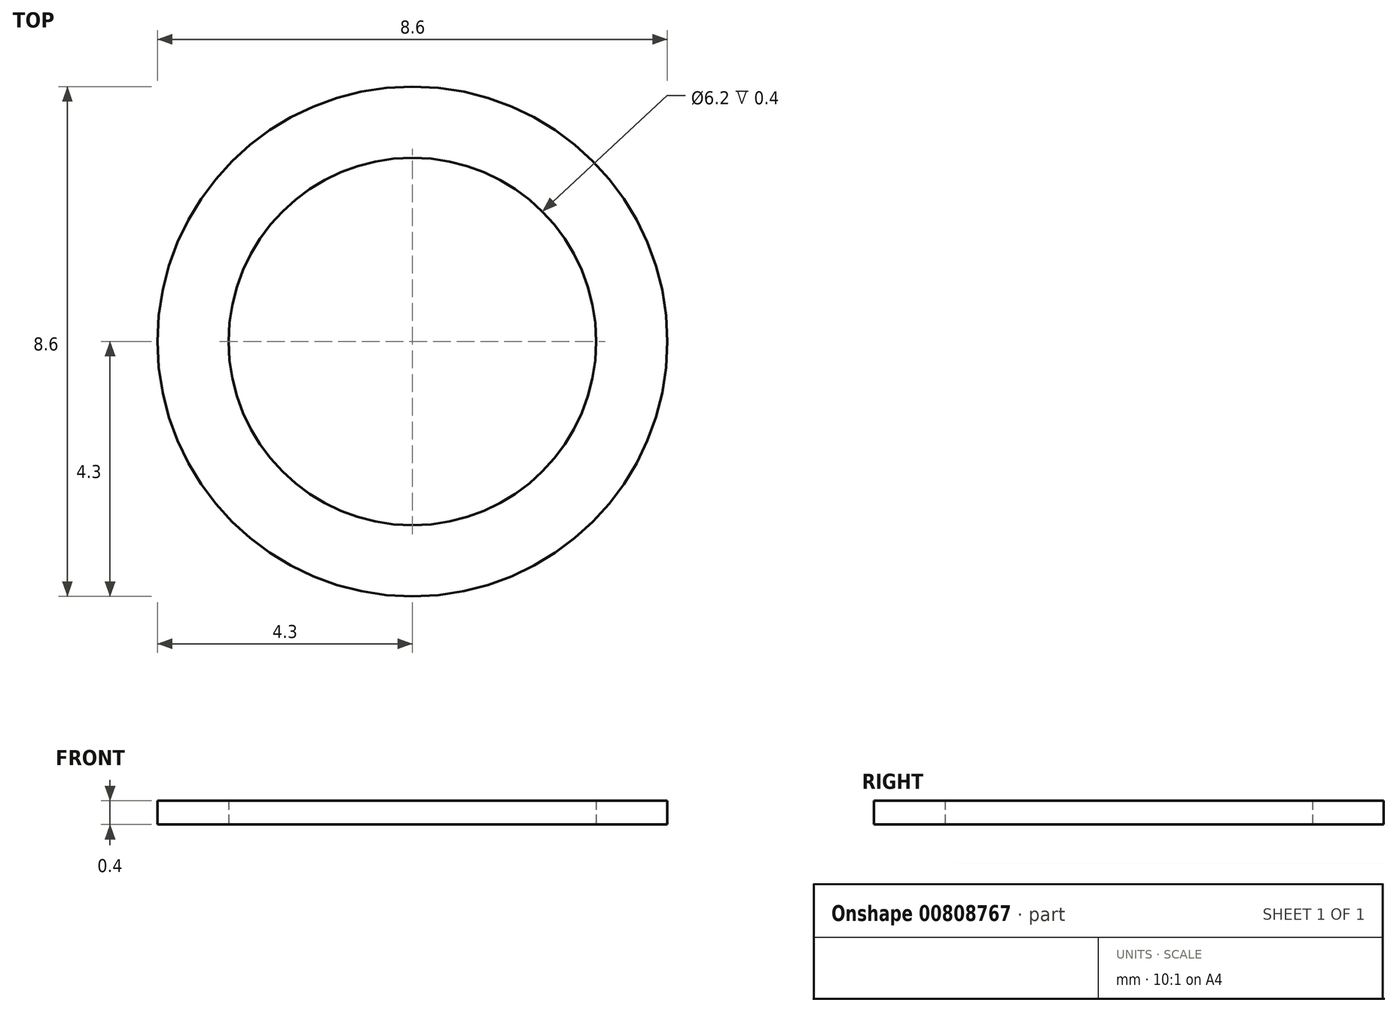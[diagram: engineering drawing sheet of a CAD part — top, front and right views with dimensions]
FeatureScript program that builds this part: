
annotation { "Feature Type Name" : "Feature", "Feature Type Description" : "" }
export const myFeature = defineFeature(function(context is Context, id is Id, definition is map)
    precondition{}
    {
        {
            var Q0;
            Q0=qCreatedBy(makeId("Top.planeOp"),FACE);
            var sketch = newSketch(context, id + "F0", { "sketchPlane" : qUnion([Q0])});
            skCircle(sketch, "E0", {"center": v(0, 0) * mm, "radius": 4.3 * mm});
            skCircle(sketch, "E1", {"center": v(0, 0) * mm, "radius": 3.1 * mm});
            skSolve(sketch);
        }
        {
            var Q0;
            Q0 = qSketchRegion(id + "F0", true);
            extrude(context, id + "F1", {"entities" : qUnion([Q0]), "depth" : 0.4 * mm, "offsetDistance" : 25 * mm});
        }
    });
